# Revit family: 444
name_source: partatom
category: Plumbing Fixtures
units: mm (PartAtom-declared; Revit-internal decimal feet)

## family parameters
Always vertical = Yes
Cut with Voids When Loaded = No
OmniClass Number = 23.45.00.00
OmniClass Title = Sanitary, Laundry, and Cleaning Equipment
Part Type = Normal
Room Calculation Point = No
Round Connector Dimension = Use Radius
Shared = No
Work Plane-Based = No

## types (1)
- 444
    Body = Iron, Cast
    CW Connection = Yes
    Default Elevation = 0"
    Description = COLADERA DE CUPULA PARA AZOTEA CONEXIÓN PARA TUBO 102 mm (4") PARA ROSCAR
    Documentation = https://www.helvex.com.mx
    Dome = Iron, Cast
    Fitting = 4" - 8 NPSM
    Grid Drain = Iron, Cast
    Manufacturer = Helvex
    Model = 444
    Total Diameter = 8"
    Total Height = 9"
    Type Comments = COLADERA DE CUPULA PARA AZOTEA CONEXIÓN PARA TUBO 102 mm (4") PARA ROSCAR
    URL = https://www.helvex.com.mx
    Vent Connection = No

## geometry (parser evidence)
native form markers: Sweep x3
no freeform markers — native parametric forms only
